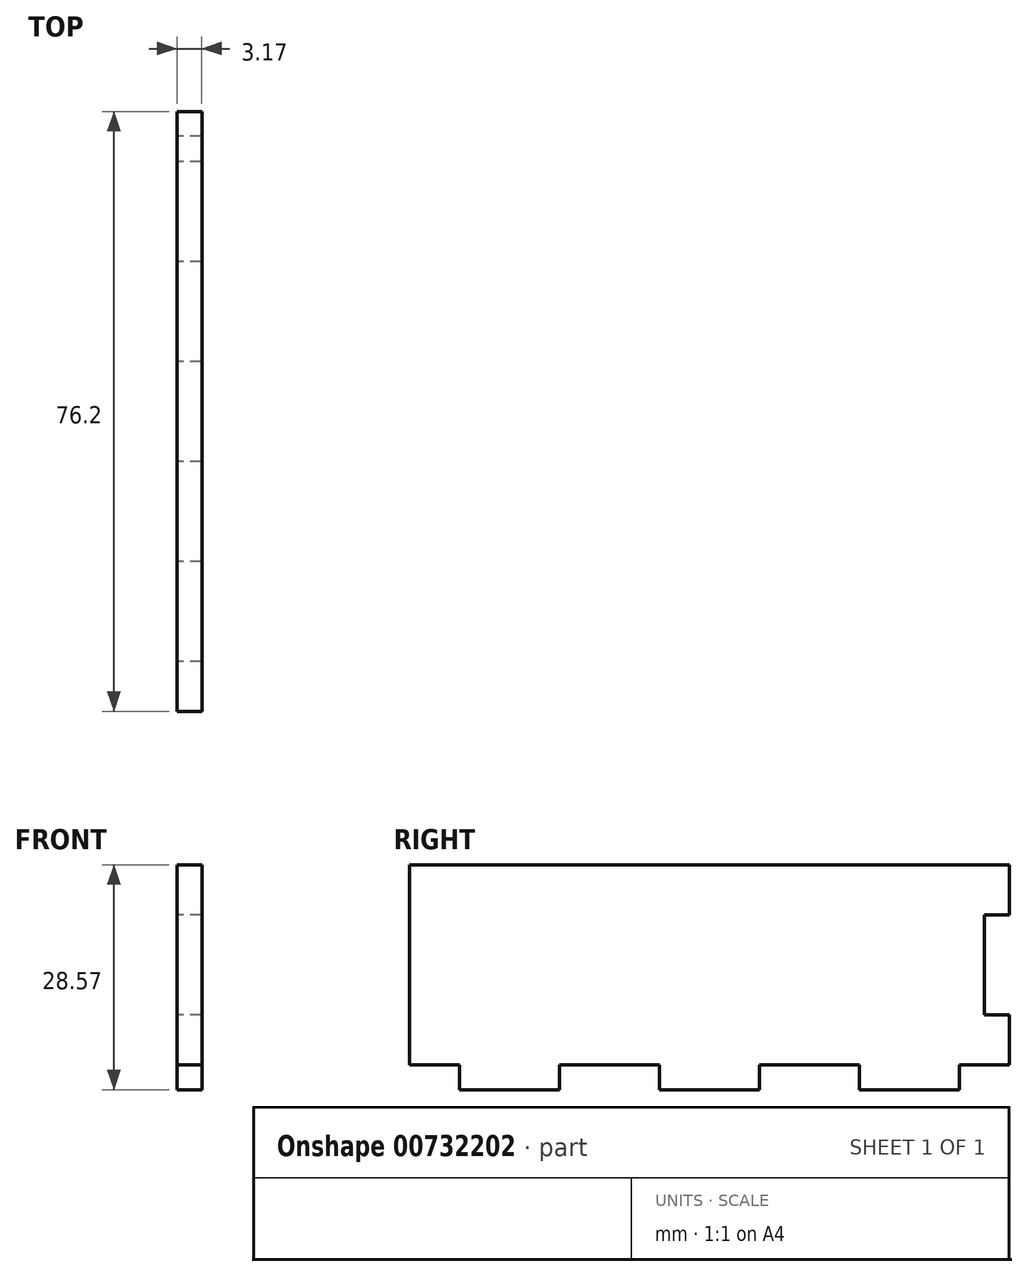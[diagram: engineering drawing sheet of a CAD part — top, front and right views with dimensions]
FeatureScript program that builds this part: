
annotation { "Feature Type Name" : "Feature", "Feature Type Description" : "" }
export const myFeature = defineFeature(function(context is Context, id is Id, definition is map)
    precondition{}
    {
        {
            var Q0;
            Q0=qCreatedBy(makeId("Right.planeOp"),FACE);
            var sketch = newSketch(context, id + "F0", { "sketchPlane" : qUnion([Q0])});
            skLineSegment(sketch, "E0", {"start": v(0, 0) * mm, "end": v(-63.5, 0) * mm});
            skLineSegment(sketch, "E1", {"start": v(-63.5, 0) * mm, "end": v(-63.5, 3.17) * mm});
            skLineSegment(sketch, "E2", {"start": v(-63.5, 3.17) * mm, "end": v(-69.85, 3.17) * mm});
            skLineSegment(sketch, "E3", {"start": v(0, 0) * mm, "end": v(0, 3.18) * mm});
            skLineSegment(sketch, "E4", {"start": v(0, 3.18) * mm, "end": v(6.35, 3.18) * mm});
            skLineSegment(sketch, "E5", {"start": v(6.35, 3.18) * mm, "end": v(6.35, 28.58) * mm});
            skLineSegment(sketch, "E6", {"start": v(6.35, 28.58) * mm, "end": v(-69.85, 28.58) * mm});
            skLineSegment(sketch, "E7", {"start": v(-69.85, 28.58) * mm, "end": v(-69.85, 3.17) * mm});
            skLineSegment(sketch, "E8", {"start": v(-63.5, 0) * mm, "end": v(-50.8, 0) * mm});
            skLineSegment(sketch, "E9", {"start": v(-50.8, 0) * mm, "end": v(-50.8, 3.17) * mm});
            skLineSegment(sketch, "E10", {"start": v(-50.8, 3.17) * mm, "end": v(-38.1, 3.17) * mm});
            skLineSegment(sketch, "E11", {"start": v(-38.1, 3.17) * mm, "end": v(-38.1, 0) * mm});
            skLineSegment(sketch, "E12", {"start": v(-38.1, 0) * mm, "end": v(-25.4, 0) * mm});
            skLineSegment(sketch, "E13", {"start": v(-25.4, 0) * mm, "end": v(-25.4, 3.17) * mm});
            skLineSegment(sketch, "E14", {"start": v(-25.4, 3.17) * mm, "end": v(-12.7, 3.17) * mm});
            skLineSegment(sketch, "E15", {"start": v(-12.7, 3.17) * mm, "end": v(-12.7, 0) * mm});
            skLineSegment(sketch, "E16", {"start": v(6.35, 28.58) * mm, "end": v(6.35, 22.23) * mm});
            skLineSegment(sketch, "E17", {"start": v(6.35, 22.23) * mm, "end": v(3.18, 22.23) * mm});
            skLineSegment(sketch, "E18", {"start": v(3.18, 22.23) * mm, "end": v(3.18, 9.53) * mm});
            skLineSegment(sketch, "E19", {"start": v(3.18, 9.53) * mm, "end": v(6.35, 9.53) * mm});
            skSolve(sketch);
        }
        {
            var Q0;
            {var subQ8=sQuery(id+"F0.wireOp",EDGE,"E1");Q0=makeQuery(id+"F0.imprint","IMPRINT",FACE,{"disambiguationData":[TD([[makeQuery(id+"F0.imprint","IMPRINT",EDGE,{"derivedFrom":subQ8}),-1.0]])]});}
            extrude(context, id + "F1", {"entities" : qUnion([Q0]), "depth" : 3.17 * mm, "offsetDistance" : 25.4 * mm});
        }
    });
